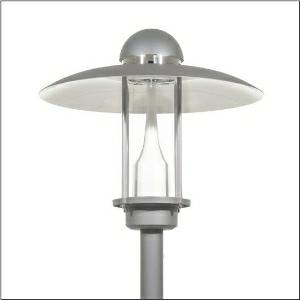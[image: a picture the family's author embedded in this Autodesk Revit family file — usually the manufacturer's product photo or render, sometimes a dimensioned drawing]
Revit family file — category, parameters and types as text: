
# Revit family: city-light_elegance_iq___p1_0a_5xa5265ff14h_a346
name_source: partatom
category: Lighting Fixtures
units: mm (PartAtom-declared; Revit-internal decimal feet)

## family parameters
Cut with Voids When Loaded = No
Host = Face
Light Source = No
Part Type = Normal
Room Calculation Point = No
Round Connector Dimension = Use Diameter
Shared = No

## types (1)
- --- (1 x LED, 1440 lm, 10.5 W, 3000K)
    Apparent Load = 11 VA
    CIE Flux Codes = 32 62 91 97 100
    Color Rendering = 70
    Color Temperature = 3000K
    Default Elevation = 1800 mm
    Description = City-Light Elegance iQ, mast luminaire, Module 540 iQ-SR, primary light control with 3 zone facetted reflector, of plastic, silver coated, highly specular, structured, primary optical cover: cover, of PMMA, transparent, light distribution: P1.0a, light emission: direct distribution, primary light characteristic: strongly asymmetric, installation type: post-top, LED, High Power LED, rated luminous flux: 1.440lm, luminous efficacy: 137lm/W, light colour: 730, colour temperature: 3000K, control gear: ECG iQ, control: Auto-Match, Temp-Guard, Lumen-Switch, Night-Set, Smart-Wire, Light-Fading, Desk-Remote (wireless, voltage-free reading and setting of iQ features in the workshop via application-optimized NFC function/RFID function), optimised constant luminous flux control (CLO 2.0), Street-Remote, presetting dimming logarithmic, with terminal, 6-pole, max. 2.5mm², mains connection: 220..240V, AC, 50/60Hz, start of lifetime: 11W, end of lifetime: 11W, reduction: 5W, luminaire housing, upper part, of aluminium, coated, Siteco® metallic grey (DB 702S), diameter: 750mm, height: 675mm, spigot size: d x l = 76 x 70mm (post-top) | with reducer (optional accessory) 60 x 70mm, post-top mast mounting element, of diecast aluminium, coated, Siteco® metallic grey (DB 702S), Module 540 iQ-SR, traffic white (RAL 9016), equipment: standard, protection rating (complete): IP65, insulation class (complete): insulation class II (safety insulation), certification: CE, ENEC, VDE, packaging unit: 1 piece

Light Distribution: P1.0a
    Height = 675 mm
    Lamp = 1 x LED
    Lamp Light Flux = 1440 lm
    Lamp Power = 10.5 W
    Lamp count = 1
    Length = 750 mm
    Luminous efficacy = 137 lm/W
    Manufacturer = Siteco
    ModVariant = No
    Model = 5XA5265FF14H
    Number of Poles = 1
    OnlyDefault = Yes
    Power Factor = 1
    Product Name = City-Light Elegance iQ | P1.0a
    Product group = mast luminaire | pylon top
    ProductGroupID = 6100
    Protection Class = Protection class II
    Protection Degree = IP 65
    RLX_Detail_Level = 1
    RlxData = <blob elided: 101461 chars, md5=bbd82613>
    Socket = socket
    Standby Power = 0 W
    System Light Flux = 1440 lm
    System Power = 11 W
    Type Comments = factory setting: luminous flux: 100 % | dim-lin: 254 | 419 mA
    Type Image = l_1006912.jpg
    URL = http://relux.com
    VarID = @adj_070971
    Voltage = 0 V
    Weight = 0.00 kg
    Width = 0 mm  [stored 0 ft]

note: [stored X ft] marks values corroborated as IEEE doubles in the binary element streams (Revit-internal decimal feet)

## geometry (parser evidence)
native form markers: Blend x4, Sweep x9
no freeform markers — native parametric forms only
